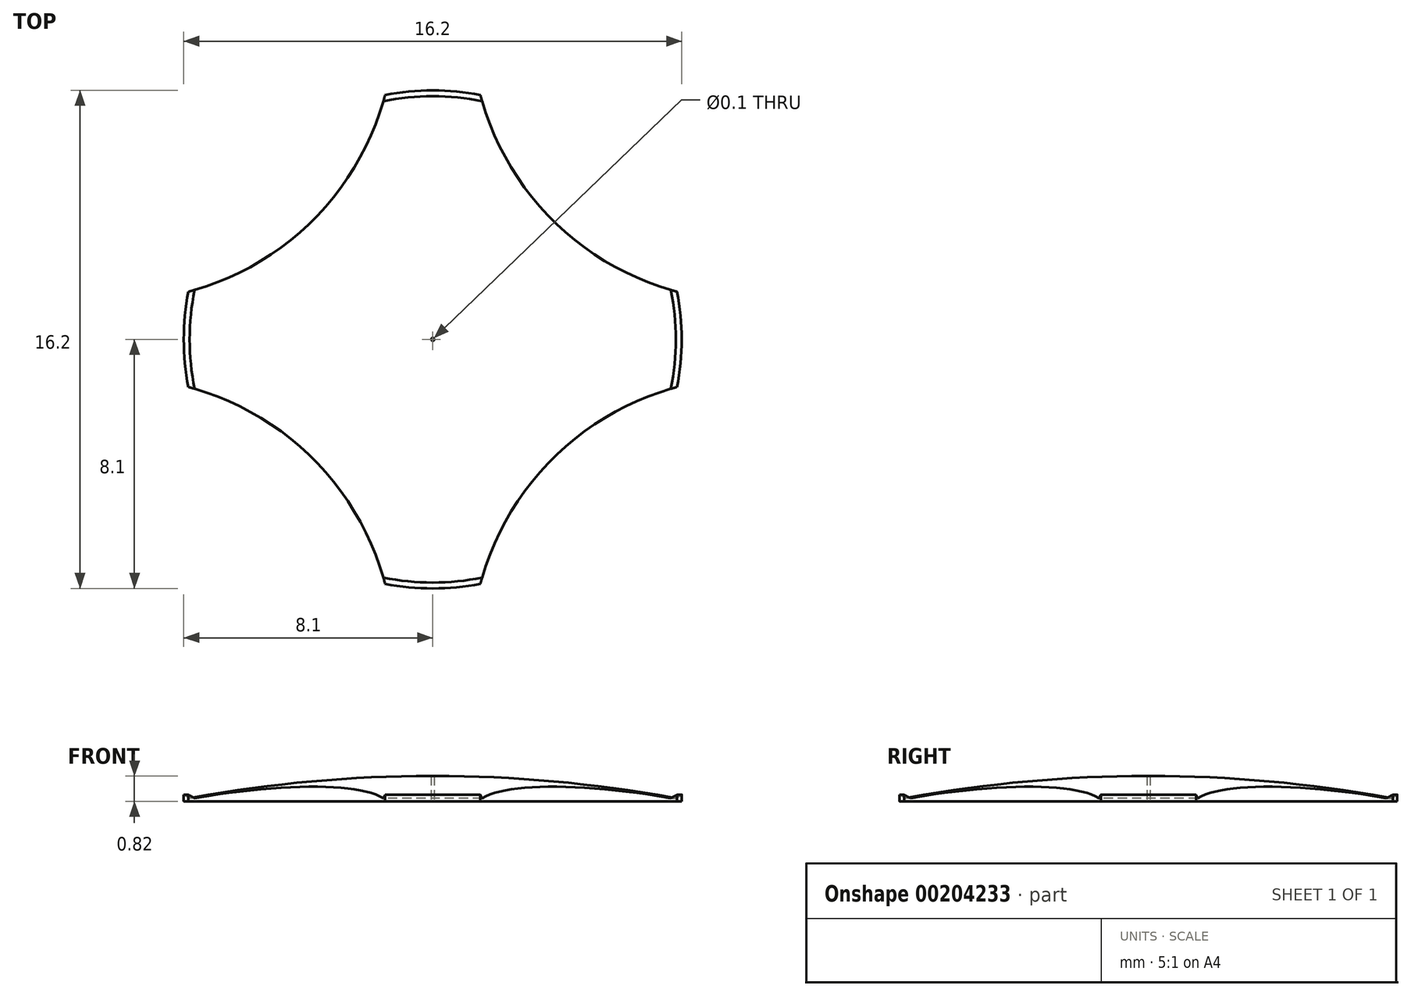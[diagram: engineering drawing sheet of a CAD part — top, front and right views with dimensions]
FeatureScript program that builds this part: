
annotation { "Feature Type Name" : "Feature", "Feature Type Description" : "" }
export const myFeature = defineFeature(function(context is Context, id is Id, definition is map)
    precondition{}
    {
        {
            var Q0;
            Q0=qCreatedBy(makeId("Front.planeOp"),FACE);
            var sketch = newSketch(context, id + "F0", { "sketchPlane" : qUnion([Q0])});
            skArc(sketch, "E0", {"start": v(7.9, 0.1) * mm, "mid": v(3.97, 0.64) * mm, "end": v(0, 0.82) * mm});
            skLineSegment(sketch, "E1", {"start": v(0, 0) * mm, "end": v(0, 0.82) * mm});
            skLineSegment(sketch, "E2", {"start": v(7.9, 0.1) * mm, "end": v(8.1, 0.2) * mm});
            skLineSegment(sketch, "E3", {"start": v(8.1, 0.2) * mm, "end": v(8.1, 0) * mm});
            skLineSegment(sketch, "E4", {"start": v(8.1, 0) * mm, "end": v(0, 0) * mm});
            skSolve(sketch);
        }
        {
            var Q0;
            Q0 = qSketchRegion(id + "F0", true);
            var Q1;
            Q1=sQuery(id+"F0.wireOp",EDGE,"E1");
            revolve(context, id + "F1", {"entities" : qUnion([Q0]), "axis" : qUnion([Q1]), "revolveType" : RevolveType.FULL});
        }
        {
            var Q0;
            Q0=makeQuery(id+"F1.opRevolve","SWEPT_FACE",FACE,{"disambiguationData":[OSD([sQuery(id+"F0.wireOp",EDGE,"E4")])]});
            var sketch = newSketch(context, id + "F2", { "sketchPlane" : qUnion([Q0])});
            skCircle(sketch, "E5", {"center": v(0, 0) * mm, "radius": 5.5 * mm, "construction": true});
            skLineSegment(sketch, "E6", {"start": v(0, 0) * mm, "end": v(-10.27, 10.27) * mm, "construction": true});
            skLineSegment(sketch, "E7", {"start": v(0, 0) * mm, "end": v(0, 16.1) * mm, "construction": true});
            skCircle(sketch, "E8", {"center": v(-10.27, 10.27) * mm, "radius": 9.02 * mm});
            skLineSegment(sketch, "E9", {"start": v(0, 0) * mm, "end": v(10.27, 10.27) * mm, "construction": true});
            skCircle(sketch, "E10", {"center": v(10.27, 10.27) * mm, "radius": 9.02 * mm});
            skLineSegment(sketch, "E11", {"start": v(-10.27, 10.27) * mm, "end": v(-1.55, 7.95) * mm, "construction": true});
            skLineSegment(sketch, "E12", {"start": v(10.27, 10.27) * mm, "end": v(1.55, 7.95) * mm, "construction": true});
            skLineSegment(sketch, "E13", {"start": v(0, 0) * mm, "end": v(-10.27, -10.27) * mm, "construction": true});
            skLineSegment(sketch, "E14", {"start": v(0, 0) * mm, "end": v(10.27, -10.27) * mm, "construction": true});
            skCircle(sketch, "E15", {"center": v(-10.27, -10.27) * mm, "radius": 9.02 * mm});
            skCircle(sketch, "E16", {"center": v(10.27, -10.27) * mm, "radius": 9.02 * mm});
            skSolve(sketch);
        }
        {
            var Q0;
            Q0 = qSketchRegion(id + "F2", true);
            extrude(context, id + "F3", {"entities" : qUnion([Q0]), "operationType" : NewBodyOperationType.REMOVE, "endBound" : BoundingType.THROUGH_ALL, "oppositeDirection" : true, "depth" : 25 * mm});
        }
        {
            var Q0;
            Q0=makeQuery(id+"F1.opRevolve","SWEPT_FACE",FACE,{"disambiguationData":[OSD([sQuery(id+"F0.wireOp",EDGE,"E4")])]});
            var sketch = newSketch(context, id + "F4", { "sketchPlane" : qUnion([Q0])});
            skCircle(sketch, "E17", {"center": v(0, 0) * mm, "radius": 0.05 * mm});
            skSolve(sketch);
        }
        {
            var Q0;
            Q0 = qSketchRegion(id + "F4", true);
            extrude(context, id + "F5", {"entities" : qUnion([Q0]), "operationType" : NewBodyOperationType.REMOVE, "oppositeDirection" : true, "depth" : 25 * mm});
        }
    });
